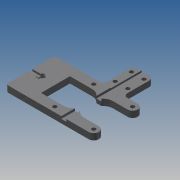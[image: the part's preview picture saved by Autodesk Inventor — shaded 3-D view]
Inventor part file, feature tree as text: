
AUTODESK INVENTOR PART (.ipt)
format: ipt  version: 2015 SP1 (Build 190203100, 203)  size: 358,912 bytes
history: native  units: mm
features: projected_geometry x16, sketch x9, extrude x9, reference x5, fillet x3, plane x1
ambient origin geometry x8: Origin, YZ Plane, XZ Plane, XY Plane, X Axis, Y Axis, Z Axis, Center Point
bodies: Body1 (feature_tree)
feature tree (43):
  sketch  "Skizze1"  dims[d0=3.1mm d1=15.5mm]
  plane  "Arbeitsebene1"
  extrude  "Extrusion5"  Depth=3.1mm
  extrude  "Extrusion8"  Depth=22.0mm
  extrude  "Extrusion9"  Depth=11.0mm
  extrude  "Extrusion10"  Depth=8.0mm
  fillet  "Rundung1"  Radius=15.0mm
  fillet  "Rundung2"  Radius=40.0mm
  extrude  "Extrusion13"  Depth=8.0mm
  extrude  "Extrusion14"  Depth=15.0mm
  extrude  "Extrusion15"  Depth=3.0mm
  extrude  "Extrusion18"  Depth=2.4mm
  extrude  "Extrusion19"  Depth=7.0mm
  fillet  "Rundung3"  Radius=3.2mm
  sketch  "Skizze4"  dims[d2=15.5mm d3=22.0mm]
  projected_geometry  "Projizierte Kontur2"
  sketch  "Skizze5"  dims[d4=16.5mm d5=11.0mm]
  projected_geometry  "Projizierte Kontur3"
  projected_geometry  "Projizierte Kontur4"
  projected_geometry  "Projizierte Kontur5"
  sketch  "Skizze6"  dims[d6=8.0mm d7=15.0mm d10=15.0mm d11=40.0mm]
  projected_geometry  "Projizierte Kontur6"
  sketch  "Skizze11"  dims[d17=8.0mm d19=8.0mm]
  projected_geometry  "Projizierte Kontur26"
  projected_geometry  "Projizierte Kontur27"
  projected_geometry  "Projizierte Kontur28"
  projected_geometry  "Projizierte Kontur29"
  projected_geometry  "Projizierte Kontur30"
  projected_geometry  "Projizierte Kontur31"
  sketch  "Skizze12"  dims[d22=35.0mm d23=15.0mm]
  projected_geometry  "Projizierte Kontur32"
  projected_geometry  "Projizierte Kontur33"
  sketch  "Skizze13"  dims[d28=5.0mm d29=0.0mm d34=3.0mm]
  projected_geometry  "Projizierte Kontur34"
  projected_geometry  "Projizierte Kontur35"
  projected_geometry  "Projizierte Kontur36"
  sketch  "Skizze18"  dims[d35=1.5mm d36=0.0mm d37=2.4mm]
  reference  "Referenz5"
  sketch  "Skizze19"  dims[d38=5.5mm d39=7.0mm d40=3.2mm d41=0.0mm d42=4.0mm d43=2.4mm d44=1.9mm d45=0.0mm d46=2.0mm d47=2.0mm d61=3.0mm d62=4.0mm d63=8.0mm d64=8.0mm d65=6.0mm d66=6.0mm d67=5.0mm d68=0.0mm d69=1.9mm d70=0.0mm d71=9.0mm d72=1.5mm d73=0.0mm d89=0.5mm d90=4.5mm d91=25.0mm d92=0.0mm d93=5.0mm d94=0.0mm d95=4.0mm]
  reference  "Referenz6"
  reference  "Referenz7"
  reference  "Referenz8"
  reference  "Referenz9"
